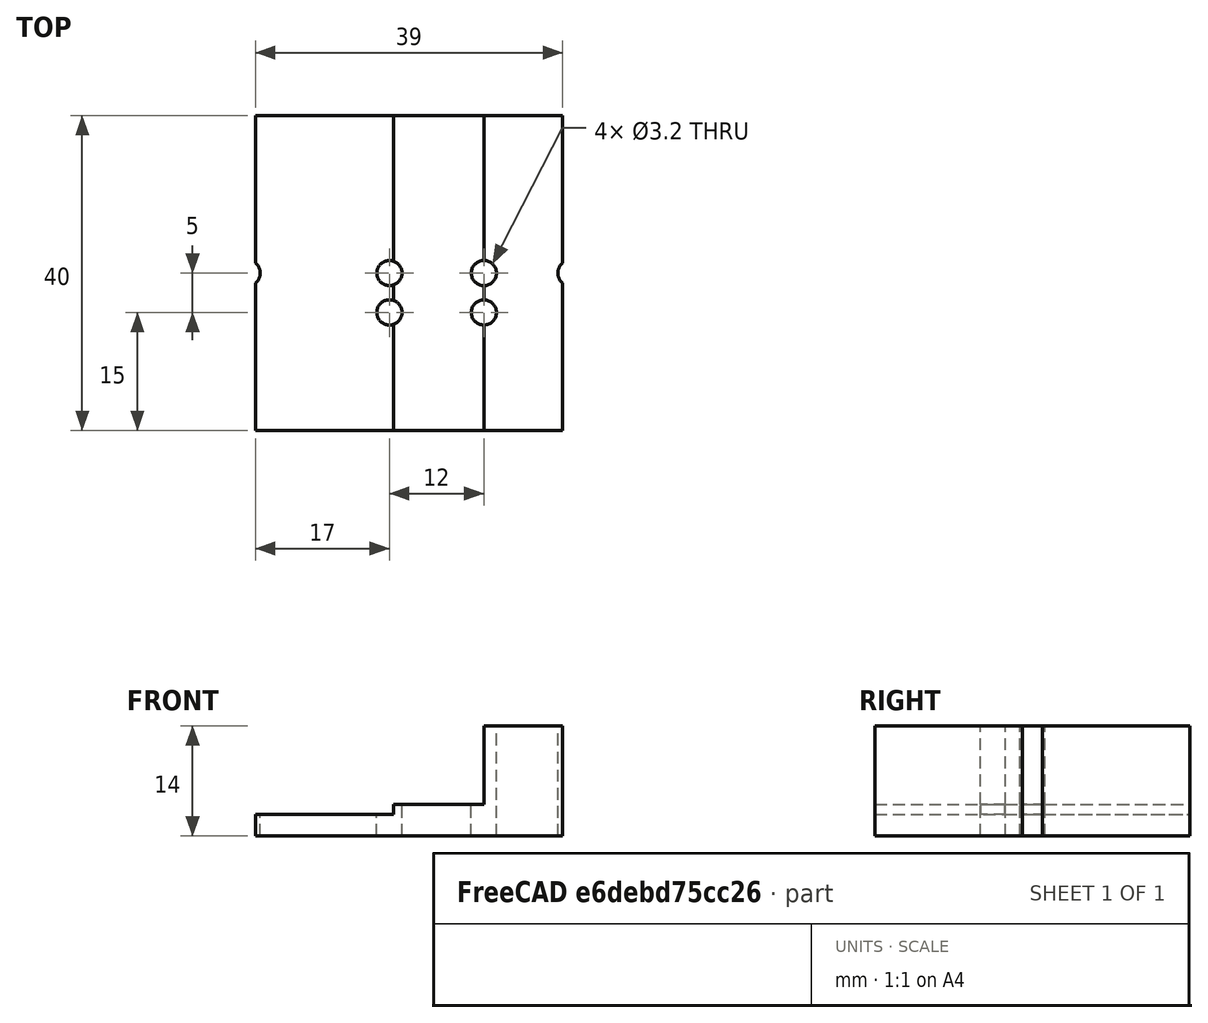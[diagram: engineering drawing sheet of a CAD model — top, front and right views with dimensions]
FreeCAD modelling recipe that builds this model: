
FCSTD DOCUMENT  (FreeCAD 0.16R6707 (Git))
Label: U3-base-2
License: All rights reserved
LicenseURL: http://en.wikipedia.org/wiki/All_rights_reserved
objects: Part::Cylinder×6, Part::Cut×6, Part::Box×3, Part::MultiFuse×1
note: 16 computed .brp shape members not serialized (recipe doc carries the construction recipe); baked Part::Feature solids carry a one-line shape summary decoded from their .brp

FEATURE [Part::Box] Box001  label="Cube001"
  Height = 2.75
  Length = 17.5
  Placement = pos=(10,50,0) rot=(0,0,1;0rad)
  Width = 40
FEATURE [Part::Box] Box002  label="Cube002"
  Height = 4
  Length = 11.5
  Placement = pos=(27.5,50,0) rot=(0,0,1;0rad)
  Width = 40
FEATURE [Part::Cylinder] Cylinder004
  Angle = 360
  Height = 10
  Placement = pos=(9,70,-5) rot=(0,0,1;0rad)
  Radius = 1.6
FEATURE [Part::Cylinder] Cylinder005
  Angle = 360
  Height = 10
  Placement = pos=(27,70,-5) rot=(0,0,1;0rad)
  Radius = 1.6
FEATURE [Part::Cylinder] Cylinder006
  Angle = 360
  Height = 10
  Placement = pos=(27,65,-5) rot=(0,0,1;0rad)
  Radius = 1.6
FEATURE [Part::Cylinder] Cylinder007
  Angle = 360
  Height = 20
  Placement = pos=(39,65,-5) rot=(0,0,1;0rad)
  Radius = 1.6
FEATURE [Part::Box] Box003  label="Cube003"
  Height = 14
  Length = 10
  Placement = pos=(39,50,0) rot=(0,0,1;0rad)
  Width = 40
FEATURE [Part::Cylinder] Cylinder008
  Angle = 360
  Height = 20
  Placement = pos=(39,70,-5) rot=(0,0,1;0rad)
  Radius = 1.6
FEATURE [Part::Cylinder] Cylinder009
  Angle = 360
  Height = 20
  Placement = pos=(50,70,-5) rot=(0,0,1;0rad)
  Radius = 1.6
FEATURE [Part::MultiFuse] Fusion
  Shapes = -> [Box001,Box002,Box003]
FEATURE [Part::Cut] Cut
  Base = -> Fusion
  Tool = -> Cylinder004
FEATURE [Part::Cut] Cut001
  Base = -> Cut
  Tool = -> Cylinder005
FEATURE [Part::Cut] Cut002
  Base = -> Cut001
  Tool = -> Cylinder006
FEATURE [Part::Cut] Cut003
  Base = -> Cut002
  Tool = -> Cylinder007
FEATURE [Part::Cut] Cut004
  Base = -> Cut003
  Tool = -> Cylinder008
FEATURE [Part::Cut] Cut005
  Base = -> Cut004
  Tool = -> Cylinder009
